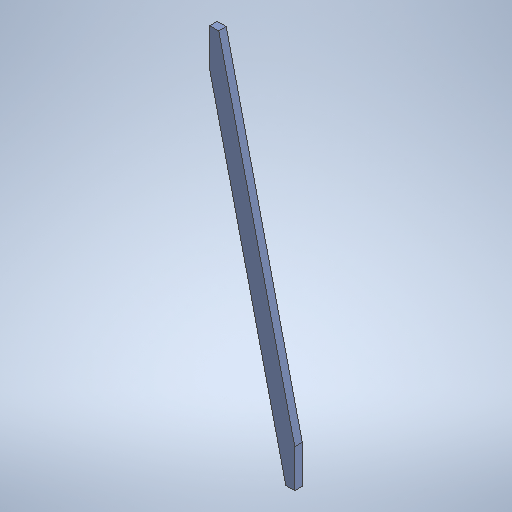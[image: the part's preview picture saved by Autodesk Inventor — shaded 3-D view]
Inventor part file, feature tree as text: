
AUTODESK INVENTOR PART (.ipt)
format: ipt  version: 2025.1 (Build 291241020, 241B)  size: 259,072 bytes
history: native  units: in
note: dims shown in document units (in); Inventor stores cm internally (conversion verified against a paired STEP export)
features: other x9, reference x6, extrude x1, sketch x1
ambient origin geometry x8: Origin, YZ Plane, XZ Plane, XY Plane, X Axis, Y Axis, Z Axis, Center Point
bodies: Solid1 (feature_tree)
feature tree (17):
  extrude  "Extrusion1"  [1 undecoded]
  sketch  "Sketch1"  dims[d4=1.5in d5=0.0in]
  reference  "Reference1"
  reference  "Reference2"
  reference  "Reference3"
  reference  "Reference4"
  reference  "Reference5"
  reference  "Reference6"
  other  "<userpath>\Documents\Tburn24\Assembly1.iam"
  other  "Assembly1.iam"
  other  "7'5x2x4:1"
  other  "6'x4x4:12"
  other  "7'5x4x4:1"
  other  "6'x4x4:14"
  other  "6'x4x4:1"
  other  "6'x4x4:23"
  other  "Finish1"
note: 1 required parameter value undecoded (feature->parameter linkage not recoverable at this tier; creation-order binding heuristic only, values carry confidence <= 0.55)
